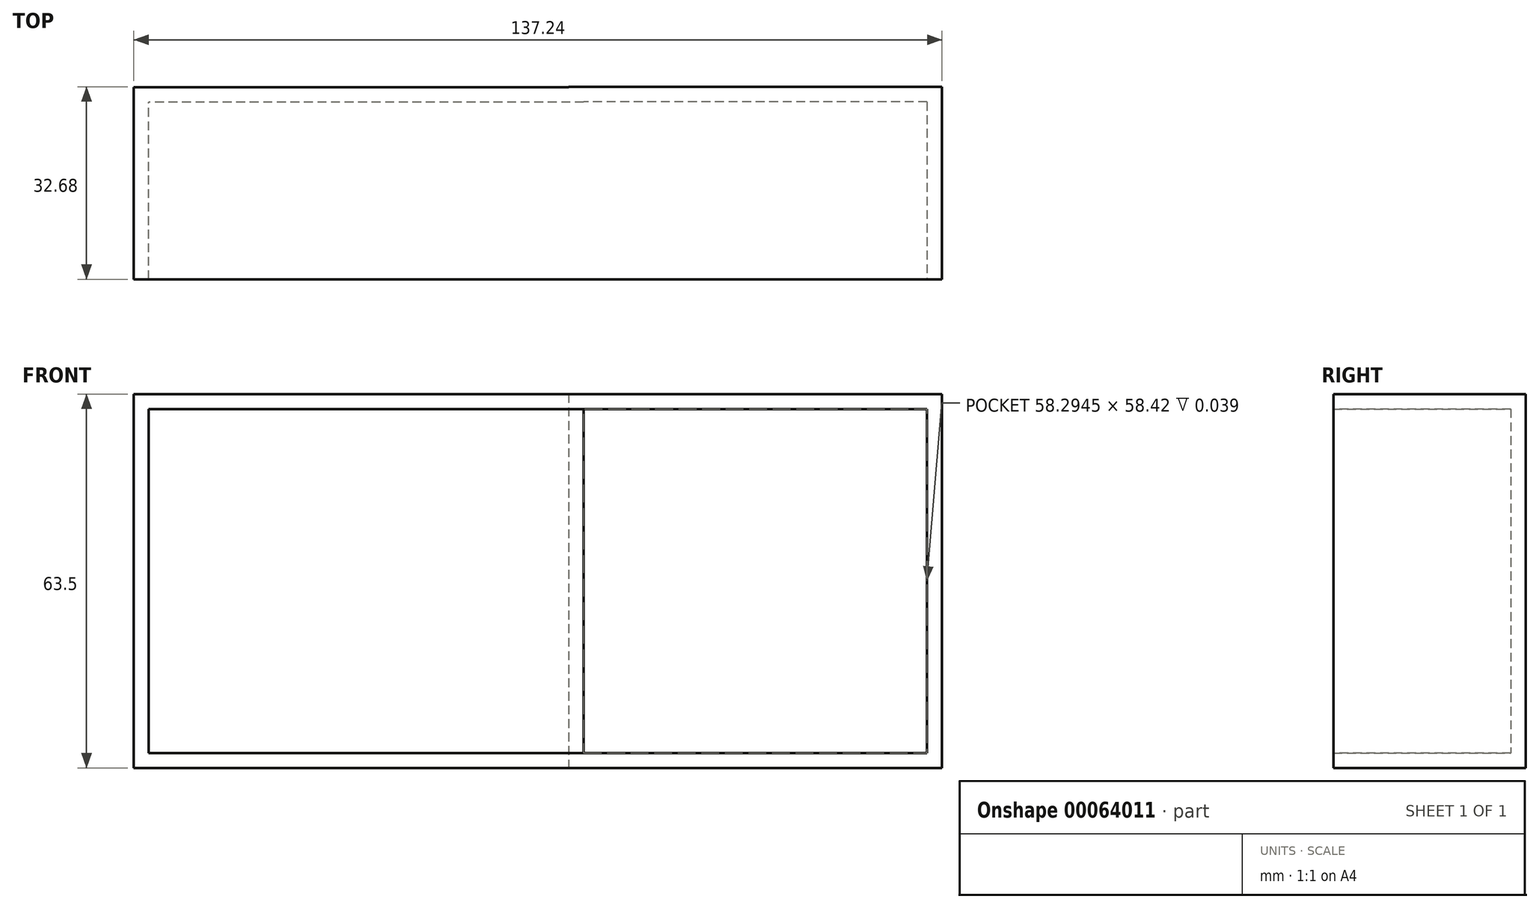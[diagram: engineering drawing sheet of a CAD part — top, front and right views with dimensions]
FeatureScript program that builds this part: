
annotation { "Feature Type Name" : "Feature", "Feature Type Description" : "" }
export const myFeature = defineFeature(function(context is Context, id is Id, definition is map)
    precondition{}
    {
        {
            var Q0;
            Q0=qCreatedBy(makeId("Top.planeOp"),FACE);
            var sketch = newSketch(context, id + "F0", { "sketchPlane" : qUnion([Q0])});
            skLineSegment(sketch, "E0.bottom", {"start": v(46.65, -51.04) * mm, "end": v(-27.22, -51.04) * mm});
            skLineSegment(sketch, "E0.top", {"start": v(46.65, -18.4) * mm, "end": v(-27.22, -18.4) * mm});
            skLineSegment(sketch, "E0.left", {"start": v(46.65, -51.04) * mm, "end": v(46.65, -18.4) * mm});
            skLineSegment(sketch, "E0.right", {"start": v(-27.22, -51.04) * mm, "end": v(-27.22, -18.4) * mm});
            skLineSegment(sketch, "E1.bottom", {"start": v(110.02, -18.36) * mm, "end": v(46.65, -18.36) * mm});
            skLineSegment(sketch, "E1.top", {"start": v(110.02, -51.04) * mm, "end": v(46.65, -51.04) * mm});
            skLineSegment(sketch, "E1.left", {"start": v(110.02, -18.36) * mm, "end": v(110.02, -51.04) * mm});
            skLineSegment(sketch, "E1.right", {"start": v(46.65, -18.36) * mm, "end": v(46.65, -51.04) * mm});
            skSolve(sketch);
        }
        {
            var Q0;
            {var subQ2=sQuery(id+"F0.wireOp",EDGE,"E1.bottom");Q0=makeQuery(id+"F0.imprint","IMPRINT",FACE,{"disambiguationData":[TD([[makeQuery(id+"F0.imprint","IMPRINT",EDGE,{"derivedFrom":subQ2}),1.0]])]});}
            var Q1;
            {var subQ0=sQuery(id+"F0.wireOp",EDGE,"E0.bottom");Q1=makeQuery(id+"F0.imprint","IMPRINT",FACE,{"disambiguationData":[TD([[makeQuery(id+"F0.imprint","IMPRINT",EDGE,{"derivedFrom":subQ0}),-1.0]])]});}
            extrude(context, id + "F1", {"entities" : qUnion([Q0, Q1]), "depth" : 63.5 * mm});
        }
        {
            var Q0;
            Q0=makeQuery(id+"F1.opExtrude","SWEPT_FACE",FACE,{"disambiguationData":[OSD([sQuery(id+"F0.wireOp",EDGE,"E0.bottom"),sQuery(id+"F0.wireOp",EDGE,"E1.top")])]});
            shell(context, id + "F2", {"entities" : qUnion([Q0]), "thickness" : 2.54 * mm});
        }
    });
